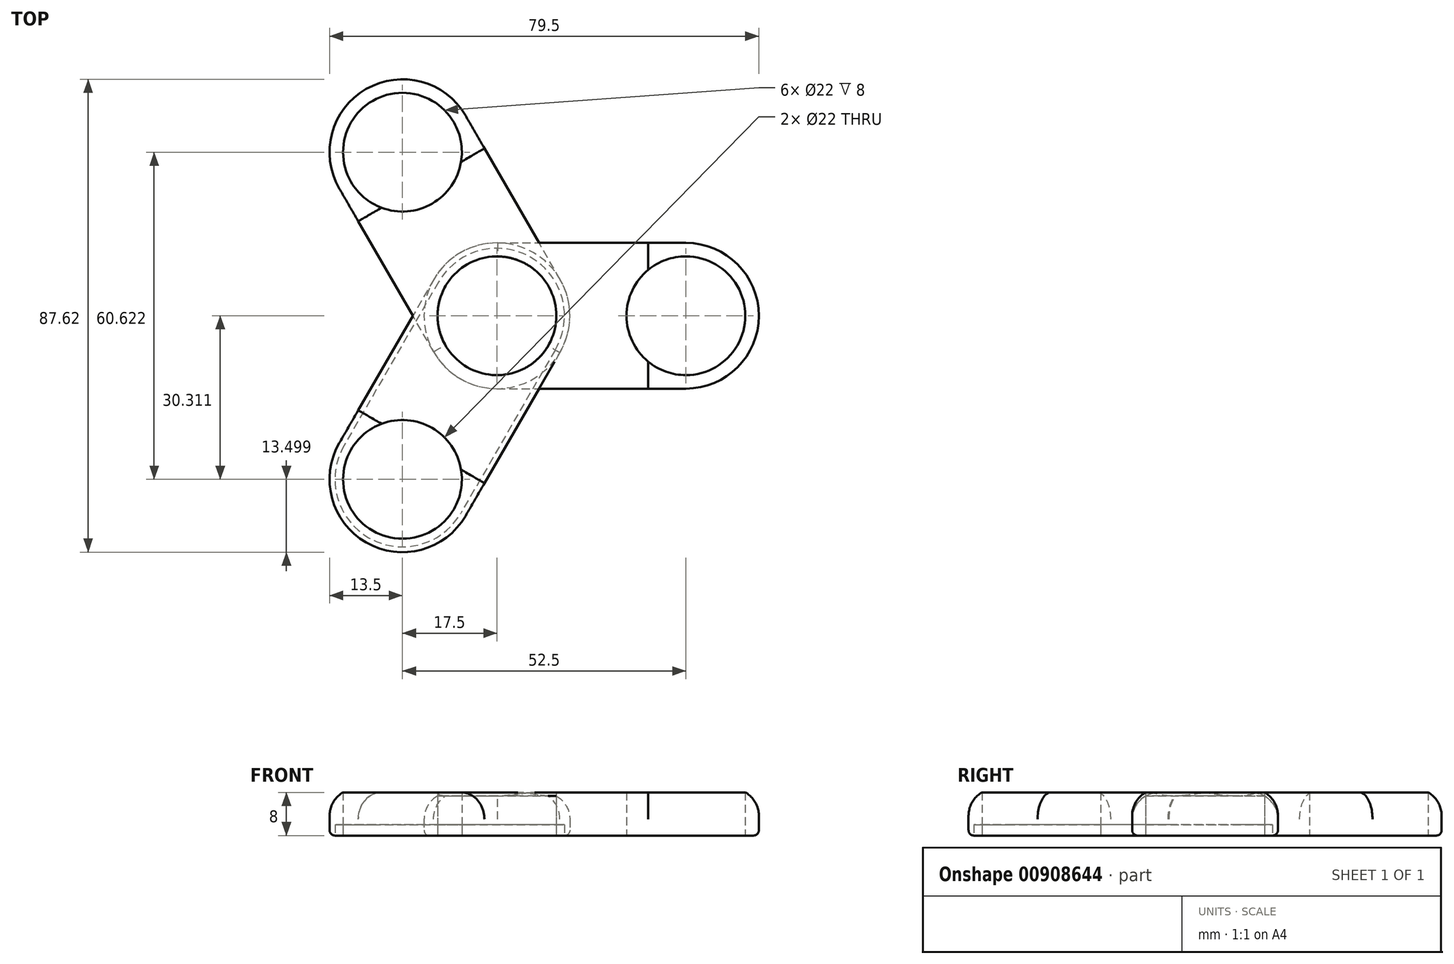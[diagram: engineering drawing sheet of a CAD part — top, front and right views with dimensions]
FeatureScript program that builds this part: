
annotation { "Feature Type Name" : "Feature", "Feature Type Description" : "" }
export const myFeature = defineFeature(function(context is Context, id is Id, definition is map)
    precondition{}
    {
        {
            var Q0;
            Q0=qCreatedBy(makeId("Top.planeOp"),FACE);
            var sketch = newSketch(context, id + "F0", { "sketchPlane" : qUnion([Q0])});
            skCircle(sketch, "E0", {"center": v(0, 0) * mm, "radius": 11 * mm});
            skCircle(sketch, "E1", {"center": v(0, 0) * mm, "radius": 13.5 * mm});
            skLineSegment(sketch, "E2", {"start": v(0, 0) * mm, "end": v(35, 0) * mm, "construction": true});
            skCircle(sketch, "E3", {"center": v(35, 0) * mm, "radius": 11 * mm});
            skCircle(sketch, "E4", {"center": v(35, 0) * mm, "radius": 13.5 * mm});
            skLineSegment(sketch, "E5", {"start": v(0.1, 13.5) * mm, "end": v(35, 13.5) * mm});
            skLineSegment(sketch, "E6", {"start": v(0, -13.5) * mm, "end": v(35, -13.5) * mm});
            skSolve(sketch);
        }
        {
            var Q0;
            Q0=makeQuery(id+"F0.imprint","IMPRINT",FACE,{"disambiguationData":[TD([[makeQuery(id+"F0.imprint","IMPRINT",EDGE,{"derivedFrom":sQuery(id+"F0.wireOp",EDGE,"E0")}),-1.0]])]});
            var Q1;
            {var subQ0=sQuery(id+"F0.wireOp",EDGE,"E5");Q1=makeQuery(id+"F0.imprint","IMPRINT",FACE,{"disambiguationData":[TD([[makeQuery(id+"F0.imprint","IMPRINT",EDGE,{"derivedFrom":subQ0}),-1.0]])]});}
            var Q2;
            Q2=makeQuery(id+"F0.imprint","IMPRINT",FACE,{"disambiguationData":[TD([[makeQuery(id+"F0.imprint","IMPRINT",EDGE,{"derivedFrom":sQuery(id+"F0.wireOp",EDGE,"E3")}),-1.0]])]});
            extrude(context, id + "F1", {"entities" : qUnion([Q0, Q1, Q2]), "depth" : 8 * mm, "offsetDistance" : 25 * mm});
        }
        {
            var Q0;
            Q0=qCreatedBy(makeId("Front.planeOp"),FACE);
            var sketch = newSketch(context, id + "F2", { "sketchPlane" : qUnion([Q0])});
            skLineSegment(sketch, "E7", {"start": v(0, 0) * mm, "end": v(0, 51.67) * mm, "construction": true});
            skSolve(sketch);
        }
        {
            var Q0;
            Q0=makeQuery(id+"F1.opExtrude","SWEPT_BODY",BODY,{"disambiguationData":[OSD([sQuery(id+"F0.wireOp",EDGE,"E0"),sQuery(id+"F0.wireOp",EDGE,"E1"),sQuery(id+"F0.wireOp",EDGE,"E3"),sQuery(id+"F0.wireOp",EDGE,"E4"),sQuery(id+"F0.wireOp",EDGE,"E5"),sQuery(id+"F0.wireOp",EDGE,"E6")])]});
            var Q1;
            Q1=sQuery(id+"F2.wireOp",EDGE,"E7");
            circularPattern(context, id + "F3", {"entities" : qUnion([Q0]), "axis" : qUnion([Q1]), "angle" : 360 * degree, "instanceCount" : 3, "equalSpace" : true});
        }
        {
            var Q0;
            Q0=makeQuery(id+"F3.opPattern","COPY",EDGE,{"derivedFrom":makeQuery(id+"F1.opExtrude","CAP_EDGE",EDGE,{"disambiguationData":[OSD([sQuery(id+"F0.wireOp",EDGE,"E5")])],"isStart":false}),"instanceName":"1"});
            var Q1;
            Q1=makeQuery(id+"F3.opPattern","COPY",EDGE,{"derivedFrom":makeQuery(id+"F1.opExtrude","CAP_EDGE",EDGE,{"disambiguationData":[OSD([sQuery(id+"F0.wireOp",EDGE,"E6")])],"isStart":false}),"instanceName":"2"});
            var Q2;
            Q2=makeQuery(id+"F1.opExtrude","CAP_EDGE",EDGE,{"disambiguationData":[OSD([sQuery(id+"F0.wireOp",EDGE,"E6")])],"isStart":false});
            fillet(context, id + "F4", {"entities" : qUnion([Q0, Q1, Q2]), "radius" : 5 * mm, "tangentPropagation" : true, "allowEdgeOverflow" : false});
        }
        {
            var Q0;
            Q0=makeQuery(id+"F1.opExtrude","CAP_EDGE",EDGE,{"disambiguationData":[OSD([sQuery(id+"F0.wireOp",EDGE,"E5")])],"isStart":true});
            var Q1;
            Q1=makeQuery(id+"F3.opPattern","COPY",EDGE,{"derivedFrom":makeQuery(id+"F1.opExtrude","CAP_EDGE",EDGE,{"disambiguationData":[OSD([sQuery(id+"F0.wireOp",EDGE,"E6")])],"isStart":true}),"instanceName":"1"});
            var Q2;
            Q2=makeQuery(id+"F3.opPattern","COPY",EDGE,{"derivedFrom":makeQuery(id+"F1.opExtrude","CAP_EDGE",EDGE,{"disambiguationData":[OSD([sQuery(id+"F0.wireOp",EDGE,"E6")])],"isStart":true}),"instanceName":"2"});
            fillet(context, id + "F6", {"entities" : qUnion([Q0, Q1, Q2]), "radius" : 1 * mm, "tangentPropagation" : true, "allowEdgeOverflow" : false});
        }
        {
            var Q0;
            Q0=makeQuery(id+"F3.opPattern","COPY",FACE,{"derivedFrom":makeQuery(id+"F1.opExtrude","CAP_FACE",FACE,{"disambiguationData":[OSD([sQuery(id+"F0.wireOp",EDGE,"E0"),sQuery(id+"F0.wireOp",EDGE,"E1"),sQuery(id+"F0.wireOp",EDGE,"E3"),sQuery(id+"F0.wireOp",EDGE,"E4"),sQuery(id+"F0.wireOp",EDGE,"E5"),sQuery(id+"F0.wireOp",EDGE,"E6")])],"isStart":true}),"instanceName":"2"});
            extrude(context, id + "F7", {"entities" : qUnion([Q0]), "oppositeDirection" : true, "depth" : 2 * mm, "offsetDistance" : 25 * mm});
        }
    });
